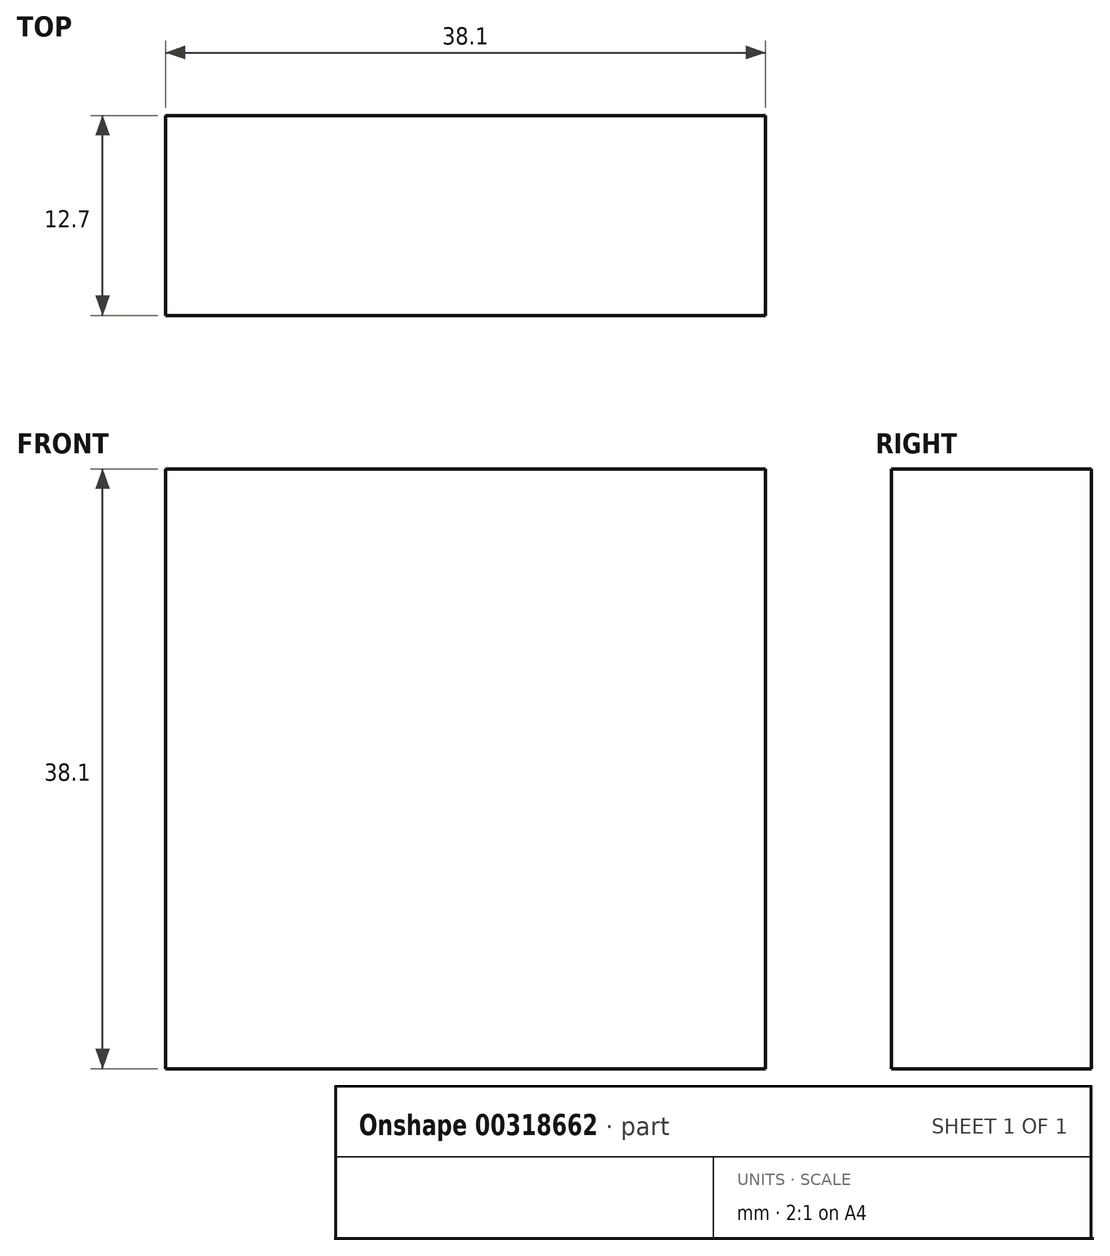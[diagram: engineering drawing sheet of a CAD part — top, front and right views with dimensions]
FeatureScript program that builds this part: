
annotation { "Feature Type Name" : "Feature", "Feature Type Description" : "" }
export const myFeature = defineFeature(function(context is Context, id is Id, definition is map)
    precondition{}
    {
        {
            var Q0;
            Q0=qCreatedBy(makeId("Front.planeOp"),FACE);
            var sketch = newSketch(context, id + "F0", { "sketchPlane" : qUnion([Q0])});
            skLineSegment(sketch, "E0.bottom", {"start": v(-19.05, 19.05) * mm, "end": v(19.05, 19.05) * mm});
            skLineSegment(sketch, "E0.top", {"start": v(-19.05, -19.05) * mm, "end": v(19.05, -19.05) * mm});
            skLineSegment(sketch, "E0.left", {"start": v(-19.05, 19.05) * mm, "end": v(-19.05, -19.05) * mm});
            skLineSegment(sketch, "E0.right", {"start": v(19.05, 19.05) * mm, "end": v(19.05, -19.05) * mm});
            skPoint(sketch, "E0.middle", {"position": v(0, 0) * mm});
            skSolve(sketch);
        }
        {
            var Q0;
            Q0=makeQuery(id+"F0.imprint","IMPRINT",FACE,{"disambiguationData":[TD([[makeQuery(id+"F0.imprint","IMPRINT",EDGE,{"derivedFrom":sQuery(id+"F0.wireOp",EDGE,"E0.bottom")}),-1.0]])]});
            extrude(context, id + "F1", {"entities" : qUnion([Q0]), "endBound" : BoundingType.SYMMETRIC, "depth" : 12.7 * mm});
        }
    });
